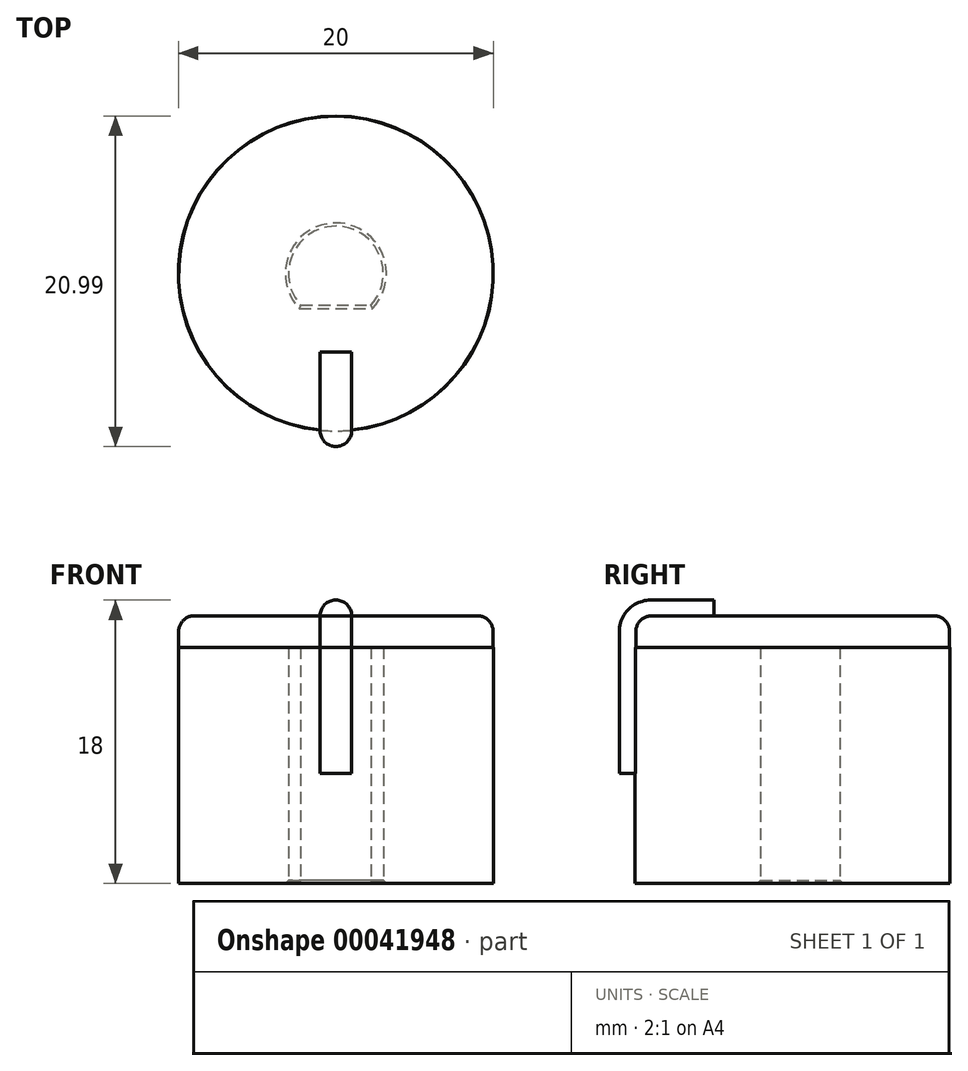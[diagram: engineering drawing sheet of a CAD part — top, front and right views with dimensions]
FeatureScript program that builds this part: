
annotation { "Feature Type Name" : "Feature", "Feature Type Description" : "" }
export const myFeature = defineFeature(function(context is Context, id is Id, definition is map)
    precondition{}
    {
        {
            var Q0;
            Q0=qCreatedBy(makeId("Top.planeOp"),FACE);
            var sketch = newSketch(context, id + "F0", { "sketchPlane" : qUnion([Q0])});
            skArc(sketch, "E0", {"start": v(2.24, -2) * mm, "mid": v(0, 3) * mm, "end": v(-2.24, -2) * mm});
            skCircle(sketch, "E1", {"center": v(0, 0) * mm, "radius": 10 * mm});
            skLineSegment(sketch, "E2", {"start": v(-2.24, -2) * mm, "end": v(2.24, -2) * mm});
            skSolve(sketch);
        }
        {
            var Q0;
            Q0=makeQuery(id+"F0.imprint","IMPRINT",FACE,{"disambiguationData":[TD([[makeQuery(id+"F0.imprint","IMPRINT",EDGE,{"derivedFrom":sQuery(id+"F0.wireOp",EDGE,"E0")}),-1.0]])]});
            extrude(context, id + "F1", {"entities" : qUnion([Q0]), "depth" : 15 * mm});
        }
        {
            var Q0;
            Q0=makeQuery(id+"F1.opExtrude","CAP_FACE",FACE,{"disambiguationData":[OSD([sQuery(id+"F0.wireOp",EDGE,"E0"),sQuery(id+"F0.wireOp",EDGE,"E1"),sQuery(id+"F0.wireOp",EDGE,"E2")])],"isStart":false});
            var sketch = newSketch(context, id + "F2", { "sketchPlane" : qUnion([Q0])});
            skCircle(sketch, "E3", {"center": v(0, 0) * mm, "radius": 9.99 * mm});
            skSolve(sketch);
        }
        {
            var Q0;
            Q0 = qSketchRegion(id + "F2", true);
            var Q1;
            Q1=makeQuery(id+"F2.imprint","IMPRINT",FACE,{"disambiguationData":[TD([[makeQuery(id+"F2.imprint","IMPRINT",EDGE,{"derivedFrom":sQuery(id+"F2.wireOp",EDGE,"E3")}),1.0]])]});
            extrude(context, id + "F9", {"entities" : qUnion([Q0, Q1]), "operationType" : NewBodyOperationType.ADD, "depth" : 2 * mm});
        }
        {
            var Q0;
            Q0=makeQuery(id+"F9.opExtrude","CAP_EDGE",EDGE,{"disambiguationData":[OSD([sQuery(id+"F2.wireOp",EDGE,"E3")])],"isStart":false});
            fillet(context, id + "F3", {"entities" : qUnion([Q0]), "radius" : 1 * mm, "tangentPropagation" : true, "allowEdgeOverflow" : false});
        }
        {
            var Q0;
            Q0=makeQuery(id+"F1.opExtrude","CAP_EDGE",EDGE,{"disambiguationData":[OSD([sQuery(id+"F0.wireOp",EDGE,"E0")])],"isStart":true});
            var Q1;
            Q1=makeQuery(id+"F1.opExtrude","CAP_EDGE",EDGE,{"disambiguationData":[OSD([sQuery(id+"F0.wireOp",EDGE,"E2")])],"isStart":true});
            chamfer(context, id + "F4", {"entities" : qUnion([Q0, Q1]), "width" : 0.2 * mm, "tangentPropagation" : true});
        }
        {
            var Q0;
            Q0=qCreatedBy(makeId("Right.planeOp"),FACE);
            var sketch = newSketch(context, id + "F5", { "sketchPlane" : qUnion([Q0])});
            skLineSegment(sketch, "E4", {"start": v(-4.99, 17) * mm, "end": v(-8.99, 17) * mm});
            skLineSegment(sketch, "E5", {"start": v(-9.99, 16) * mm, "end": v(-9.99, 7) * mm});
            skPoint(sketch, "E6.visualSharp", {"position": v(-9.99, 17) * mm});
            skArc(sketch, "E6.filletArc", {"start": v(-8.99, 17) * mm, "mid": v(-9.7, 16.7) * mm, "end": v(-9.99, 16) * mm});
            skSolve(sketch);
        }
        {
            var Q0;
            Q0=sQuery(id+"F5.wireOp",EDGE,"E5");
            var Q1;
            Q1=sQuery(id+"F5.wireOp",VERTEX,"E5.end");
            cPlane(context, id + "F6", {"entities" : qUnion([Q0, Q1]), "cplaneType" : CPlaneType.CURVE_POINT, "offset" : 150 * mm, "width" : 150 * mm, "height" : 150 * mm});
        }
        {
            var Q0;
            Q0=qCreatedBy(id+"F6.planeOp",FACE);
            var sketch = newSketch(context, id + "F7", { "sketchPlane" : qUnion([Q0])});
            skCircle(sketch, "E7", {"center": v(0, 9.99) * mm, "radius": 1 * mm});
            skSolve(sketch);
        }
        {
            var Q0;
            Q0 = qSketchRegion(id + "F7", true);
            var Q1;
            Q1=sQuery(id+"F5.wireOp",EDGE,"E5");
            var Q2;
            Q2=sQuery(id+"F5.wireOp",EDGE,"E6.filletArc");
            var Q3;
            Q3=sQuery(id+"F5.wireOp",EDGE,"E4");
            sweep(context, id + "F8", {"operationType" : NewBodyOperationType.ADD, "profiles" : qUnion([Q0]), "path" : qUnion([Q1, Q2, Q3])});
        }
    });
